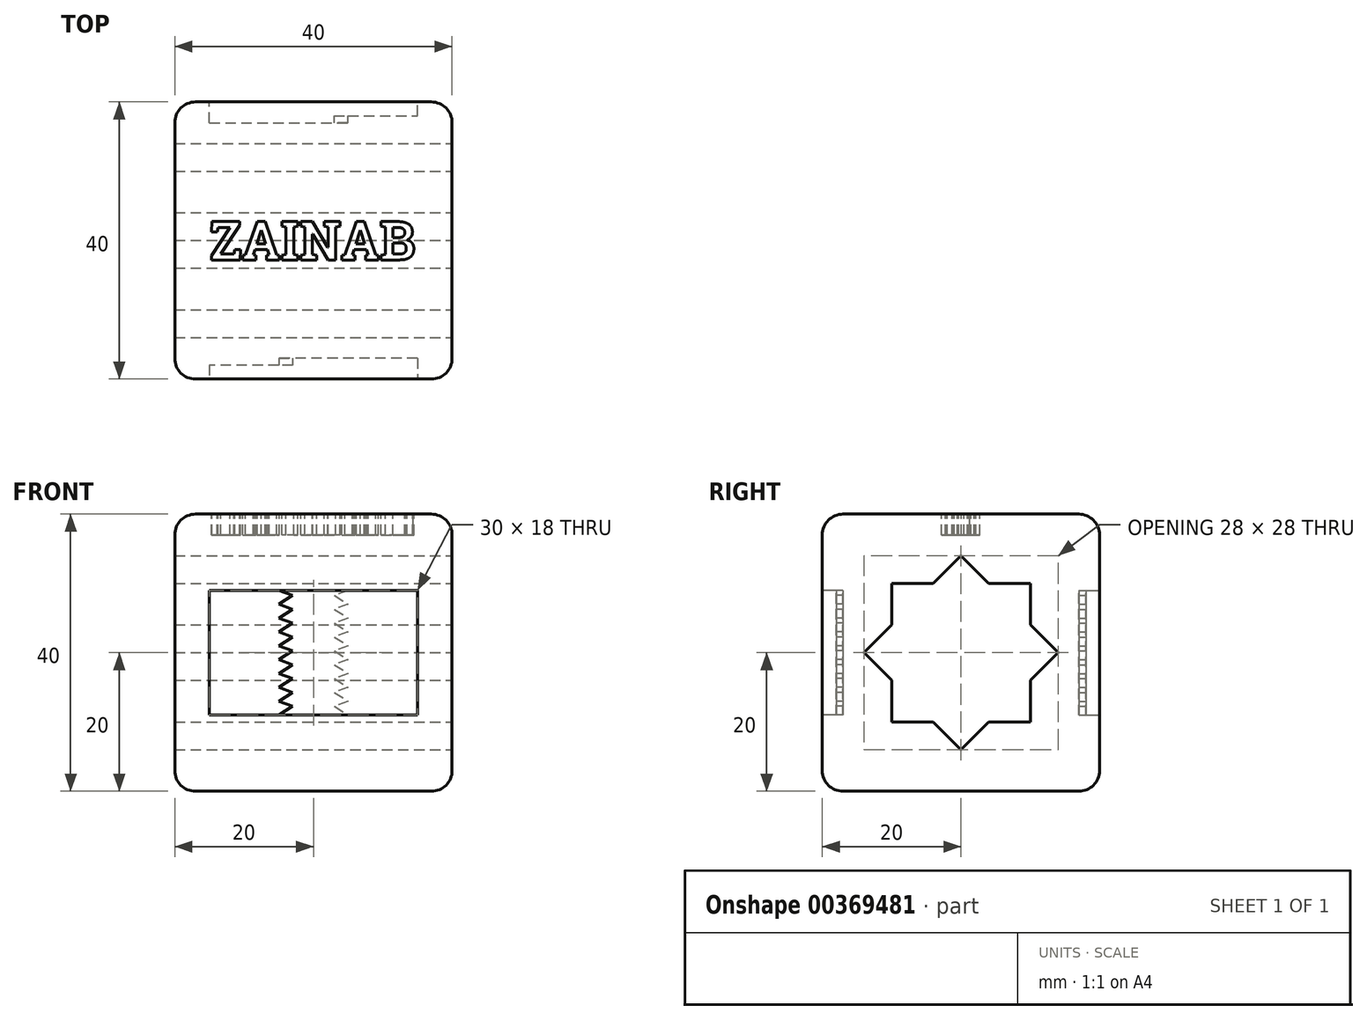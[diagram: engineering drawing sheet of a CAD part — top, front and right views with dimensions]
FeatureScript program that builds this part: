
annotation { "Feature Type Name" : "Feature", "Feature Type Description" : "" }
export const myFeature = defineFeature(function(context is Context, id is Id, definition is map)
    precondition{}
    {
        {
            var Q0;
            Q0=qCreatedBy(makeId("Front.planeOp"),FACE);
            var sketch = newSketch(context, id + "F0", { "sketchPlane" : qUnion([Q0])});
            skLineSegment(sketch, "E0.bottom", {"start": v(20, -20) * mm, "end": v(-20, -20) * mm});
            skLineSegment(sketch, "E0.top", {"start": v(20, 20) * mm, "end": v(-20, 20) * mm});
            skLineSegment(sketch, "E0.left", {"start": v(20, -20) * mm, "end": v(20, 20) * mm});
            skLineSegment(sketch, "E0.right", {"start": v(-20, -20) * mm, "end": v(-20, 20) * mm});
            skPoint(sketch, "E0.middle", {"position": v(0, 0) * mm});
            skSolve(sketch);
        }
        {
            var Q0;
            Q0 = qSketchRegion(id + "F0", true);
            extrude(context, id + "F1", {"entities" : qUnion([Q0]), "endBound" : BoundingType.SYMMETRIC, "depth" : 40 * mm});
        }
        {
            var Q0;
            Q0=makeQuery(id+"F1.opExtrude","CAP_EDGE",EDGE,{"disambiguationData":[OSD([sQuery(id+"F0.wireOp",EDGE,"E0.top")])],"isStart":false});
            var Q1;
            Q1=makeQuery(id+"F1.opExtrude","SWEPT_EDGE",EDGE,{"disambiguationData":[OSD([sQuery(id+"F0.wireOp",EDGE,"E0.top"),sQuery(id+"F0.wireOp",EDGE,"E0.left")])]});
            var Q2;
            Q2=makeQuery(id+"F1.opExtrude","CAP_EDGE",EDGE,{"disambiguationData":[OSD([sQuery(id+"F0.wireOp",EDGE,"E0.top")])],"isStart":true});
            var Q3;
            Q3=makeQuery(id+"F1.opExtrude","SWEPT_FACE",FACE,{"disambiguationData":[OSD([sQuery(id+"F0.wireOp",EDGE,"E0.top")])]});
            var Q4;
            Q4=makeQuery(id+"F1.opExtrude","SWEPT_EDGE",EDGE,{"disambiguationData":[OSD([sQuery(id+"F0.wireOp",EDGE,"E0.bottom"),sQuery(id+"F0.wireOp",EDGE,"E0.left")])]});
            var Q5;
            Q5=makeQuery(id+"F1.opExtrude","CAP_EDGE",EDGE,{"disambiguationData":[OSD([sQuery(id+"F0.wireOp",EDGE,"E0.left")])],"isStart":true});
            var Q6;
            Q6=makeQuery(id+"F1.opExtrude","CAP_EDGE",EDGE,{"disambiguationData":[OSD([sQuery(id+"F0.wireOp",EDGE,"E0.left")])],"isStart":false});
            var Q7;
            Q7=makeQuery(id+"F1.opExtrude","CAP_EDGE",EDGE,{"disambiguationData":[OSD([sQuery(id+"F0.wireOp",EDGE,"E0.bottom")])],"isStart":false});
            var Q8;
            Q8=makeQuery(id+"F1.opExtrude","CAP_EDGE",EDGE,{"disambiguationData":[OSD([sQuery(id+"F0.wireOp",EDGE,"E0.right")])],"isStart":false});
            var Q9;
            Q9=makeQuery(id+"F1.opExtrude","SWEPT_EDGE",EDGE,{"disambiguationData":[OSD([sQuery(id+"F0.wireOp",EDGE,"E0.bottom"),sQuery(id+"F0.wireOp",EDGE,"E0.right")])]});
            var Q10;
            Q10=makeQuery(id+"F1.opExtrude","CAP_EDGE",EDGE,{"disambiguationData":[OSD([sQuery(id+"F0.wireOp",EDGE,"E0.right")])],"isStart":true});
            var Q11;
            Q11=makeQuery(id+"F1.opExtrude","CAP_EDGE",EDGE,{"disambiguationData":[OSD([sQuery(id+"F0.wireOp",EDGE,"E0.bottom")])],"isStart":true});
            fillet(context, id + "F2", {"entities" : qUnion([Q0, Q1, Q2, Q3, Q4, Q5, Q6, Q7, Q8, Q9, Q10, Q11]), "radius" : 3 * mm, "tangentPropagation" : true, "allowEdgeOverflow" : false});
        }
        {
            var Q0;
            Q0=makeQuery(id+"F1.opExtrude","SWEPT_FACE",FACE,{"disambiguationData":[OSD([sQuery(id+"F0.wireOp",EDGE,"E0.left")])]});
            var sketch = newSketch(context, id + "F3", { "sketchPlane" : qUnion([Q0])});
            skLineSegment(sketch, "E1.bottom", {"start": v(10, -10) * mm, "end": v(-10, -10) * mm});
            skLineSegment(sketch, "E1.top", {"start": v(10, 10) * mm, "end": v(-10, 10) * mm});
            skLineSegment(sketch, "E1.left", {"start": v(10, -10) * mm, "end": v(10, 10) * mm});
            skLineSegment(sketch, "E1.right", {"start": v(-10, -10) * mm, "end": v(-10, 10) * mm});
            skPoint(sketch, "E1.middle", {"position": v(0, 0) * mm});
            skCircle(sketch, "E2.cCircle", {"center": v(0, 0) * mm, "radius": 14 * mm, "construction": true});
            skPoint(sketch, "E2.cCircle.perimeterSnap0", {"position": v(0, 10) * mm});
            skLineSegment(sketch, "E2.0", {"start": v(0, 14) * mm, "end": v(14, 0) * mm});
            skPoint(sketch, "E2.0.startSnap0", {"position": v(0, 10) * mm});
            skLineSegment(sketch, "E2.1", {"start": v(14, 0) * mm, "end": v(0, -14) * mm});
            skLineSegment(sketch, "E2.2", {"start": v(0, -14) * mm, "end": v(-14, 0) * mm});
            skLineSegment(sketch, "E2.3", {"start": v(-14, 0) * mm, "end": v(0, 14) * mm});
            skSolve(sketch);
        }
        {
            var Q0;
            Q0 = qSketchRegion(id + "F3", true);
            extrude(context, id + "F4", {"entities" : qUnion([Q0]), "operationType" : NewBodyOperationType.REMOVE, "endBound" : BoundingType.THROUGH_ALL, "oppositeDirection" : true, "depth" : 25 * mm});
        }
        {
            var Q0;
            Q0=makeQuery(id+"F1.opExtrude","CAP_FACE",FACE,{"disambiguationData":[OSD([sQuery(id+"F0.wireOp",EDGE,"E0.bottom"),sQuery(id+"F0.wireOp",EDGE,"E0.top"),sQuery(id+"F0.wireOp",EDGE,"E0.left"),sQuery(id+"F0.wireOp",EDGE,"E0.right")])],"isStart":false});
            var sketch = newSketch(context, id + "F5", { "sketchPlane" : qUnion([Q0])});
            skLineSegment(sketch, "E3.bottom", {"start": v(15, -9) * mm, "end": v(-15, -9) * mm});
            skLineSegment(sketch, "E3.top", {"start": v(15, 9) * mm, "end": v(-15, 9) * mm});
            skLineSegment(sketch, "E3.left", {"start": v(15, -9) * mm, "end": v(15, 9) * mm});
            skLineSegment(sketch, "E3.right", {"start": v(-15, -9) * mm, "end": v(-15, 9) * mm});
            skPoint(sketch, "E3.middle", {"position": v(0, 0) * mm});
            skLineSegment(sketch, "E4", {"start": v(-5, 9) * mm, "end": v(-3, 8.27) * mm});
            skLineSegment(sketch, "E5", {"start": v(-3, 8.27) * mm, "end": v(-5, 7) * mm});
            skLineSegment(sketch, "E6.0.1.0", {"start": v(-5, 7) * mm, "end": v(-3, 6.27) * mm});
            skLineSegment(sketch, "E6.0.1.1", {"start": v(-3, 6.27) * mm, "end": v(-5, 5) * mm});
            skLineSegment(sketch, "E6.0.2.0", {"start": v(-5, 5) * mm, "end": v(-3, 4.27) * mm});
            skLineSegment(sketch, "E6.0.2.1", {"start": v(-3, 4.27) * mm, "end": v(-5, 3) * mm});
            skLineSegment(sketch, "E6.0.3.0", {"start": v(-5, 3) * mm, "end": v(-3, 2.27) * mm});
            skLineSegment(sketch, "E6.0.3.1", {"start": v(-3, 2.27) * mm, "end": v(-5, 1) * mm});
            skLineSegment(sketch, "E6.0.4.0", {"start": v(-5, 1) * mm, "end": v(-3, 0.27) * mm});
            skLineSegment(sketch, "E6.0.4.1", {"start": v(-3, 0.27) * mm, "end": v(-5, -1) * mm});
            skLineSegment(sketch, "E6.0.5.0", {"start": v(-5, -1) * mm, "end": v(-3, -1.73) * mm});
            skLineSegment(sketch, "E6.0.5.1", {"start": v(-3, -1.73) * mm, "end": v(-5, -3) * mm});
            skLineSegment(sketch, "E6.0.6.0", {"start": v(-5, -3) * mm, "end": v(-3, -3.73) * mm});
            skLineSegment(sketch, "E6.0.6.1", {"start": v(-3, -3.73) * mm, "end": v(-5, -5) * mm});
            skLineSegment(sketch, "E6.0.7.0", {"start": v(-5, -5) * mm, "end": v(-3, -5.73) * mm});
            skLineSegment(sketch, "E6.0.7.1", {"start": v(-3, -5.73) * mm, "end": v(-5, -7) * mm});
            skLineSegment(sketch, "E6.0.8.0", {"start": v(-5, -7) * mm, "end": v(-3, -7.73) * mm});
            skLineSegment(sketch, "E6.0.8.1", {"start": v(-3, -7.73) * mm, "end": v(-5, -9) * mm});
            skLineSegment(sketch, "E6.direction1", {"start": v(-5, 9) * mm, "end": v(20, 9) * mm, "construction": true});
            skLineSegment(sketch, "E6.direction2", {"start": v(-5, 9) * mm, "end": v(-5, 7) * mm, "construction": true});
            skSolve(sketch);
        }
        {
            var Q0;
            {var subQ0=sQuery(id+"F5.wireOp",EDGE,"E3.right");Q0=makeQuery(id+"F5.imprint","IMPRINT",FACE,{"disambiguationData":[TD([[makeQuery(id+"F5.imprint","IMPRINT",EDGE,{"derivedFrom":subQ0}),-1.0]])]});}
            extrude(context, id + "F6", {"entities" : qUnion([Q0]), "operationType" : NewBodyOperationType.REMOVE, "oppositeDirection" : true, "depth" : 2 * mm});
        }
        {
            var Q0;
            {var subQ0=sQuery(id+"F5.wireOp",EDGE,"E3.left");Q0=makeQuery(id+"F5.imprint","IMPRINT",FACE,{"disambiguationData":[TD([[makeQuery(id+"F5.imprint","IMPRINT",EDGE,{"derivedFrom":subQ0}),1.0]])]});}
            extrude(context, id + "F7", {"entities" : qUnion([Q0]), "operationType" : NewBodyOperationType.REMOVE, "oppositeDirection" : true, "depth" : 3 * mm});
        }
        {
            var Q0;
            Q0=makeQuery(id+"F1.opExtrude","CAP_FACE",FACE,{"disambiguationData":[OSD([sQuery(id+"F0.wireOp",EDGE,"E0.bottom"),sQuery(id+"F0.wireOp",EDGE,"E0.top"),sQuery(id+"F0.wireOp",EDGE,"E0.left"),sQuery(id+"F0.wireOp",EDGE,"E0.right")])],"isStart":true});
            var sketch = newSketch(context, id + "F8", { "sketchPlane" : qUnion([Q0])});
            skLineSegment(sketch, "E7.bottom", {"start": v(15, -9) * mm, "end": v(-15, -9) * mm});
            skLineSegment(sketch, "E7.top", {"start": v(15, 9) * mm, "end": v(-15, 9) * mm});
            skLineSegment(sketch, "E7.left", {"start": v(15, -9) * mm, "end": v(15, 9) * mm});
            skLineSegment(sketch, "E7.right", {"start": v(-15, -9) * mm, "end": v(-15, 9) * mm});
            skPoint(sketch, "E7.middle", {"position": v(0, 0) * mm});
            skLineSegment(sketch, "E8", {"start": v(-5, 9) * mm, "end": v(-3, 8.27) * mm});
            skLineSegment(sketch, "E9", {"start": v(-3, 8.27) * mm, "end": v(-5, 7) * mm});
            skLineSegment(sketch, "E10.0.1.0", {"start": v(-5, 7) * mm, "end": v(-3, 6.27) * mm});
            skLineSegment(sketch, "E10.0.1.1", {"start": v(-3, 6.27) * mm, "end": v(-5, 5) * mm});
            skLineSegment(sketch, "E10.0.2.0", {"start": v(-5, 5) * mm, "end": v(-3, 4.27) * mm});
            skLineSegment(sketch, "E10.0.2.1", {"start": v(-3, 4.27) * mm, "end": v(-5, 3) * mm});
            skLineSegment(sketch, "E10.0.3.0", {"start": v(-5, 3) * mm, "end": v(-3, 2.27) * mm});
            skLineSegment(sketch, "E10.0.3.1", {"start": v(-3, 2.27) * mm, "end": v(-5, 1) * mm});
            skLineSegment(sketch, "E10.0.4.0", {"start": v(-5, 1) * mm, "end": v(-3, 0.27) * mm});
            skLineSegment(sketch, "E10.0.4.1", {"start": v(-3, 0.27) * mm, "end": v(-5, -1) * mm});
            skLineSegment(sketch, "E10.0.5.0", {"start": v(-5, -1) * mm, "end": v(-3, -1.73) * mm});
            skLineSegment(sketch, "E10.0.5.1", {"start": v(-3, -1.73) * mm, "end": v(-5, -3) * mm});
            skLineSegment(sketch, "E10.0.6.0", {"start": v(-5, -3) * mm, "end": v(-3, -3.73) * mm});
            skLineSegment(sketch, "E10.0.6.1", {"start": v(-3, -3.73) * mm, "end": v(-5, -5) * mm});
            skLineSegment(sketch, "E10.0.7.0", {"start": v(-5, -5) * mm, "end": v(-3, -5.73) * mm});
            skLineSegment(sketch, "E10.0.7.1", {"start": v(-3, -5.73) * mm, "end": v(-5, -7) * mm});
            skLineSegment(sketch, "E10.0.8.0", {"start": v(-5, -7) * mm, "end": v(-3, -7.73) * mm});
            skLineSegment(sketch, "E10.0.8.1", {"start": v(-3, -7.73) * mm, "end": v(-5, -9) * mm});
            skLineSegment(sketch, "E10.direction1", {"start": v(-5, 9) * mm, "end": v(20, 9) * mm, "construction": true});
            skLineSegment(sketch, "E10.direction2", {"start": v(-5, 9) * mm, "end": v(-5, 7) * mm, "construction": true});
            skSolve(sketch);
        }
        {
            var Q0;
            {var subQ0=sQuery(id+"F8.wireOp",EDGE,"E7.right");Q0=makeQuery(id+"F8.imprint","IMPRINT",FACE,{"disambiguationData":[TD([[makeQuery(id+"F8.imprint","IMPRINT",EDGE,{"derivedFrom":subQ0}),-1.0]])]});}
            extrude(context, id + "F9", {"entities" : qUnion([Q0]), "operationType" : NewBodyOperationType.REMOVE, "oppositeDirection" : true, "depth" : 2 * mm});
        }
        {
            var Q0;
            {var subQ0=sQuery(id+"F8.wireOp",EDGE,"E7.left");Q0=makeQuery(id+"F8.imprint","IMPRINT",FACE,{"disambiguationData":[TD([[makeQuery(id+"F8.imprint","IMPRINT",EDGE,{"derivedFrom":subQ0}),1.0]])]});}
            extrude(context, id + "F10", {"entities" : qUnion([Q0]), "operationType" : NewBodyOperationType.REMOVE, "oppositeDirection" : true, "depth" : 3 * mm});
        }
        {
            var Q0;
            Q0=makeQuery(id+"F1.opExtrude","SWEPT_FACE",FACE,{"disambiguationData":[OSD([sQuery(id+"F0.wireOp",EDGE,"E0.top")])]});
            var sketch = newSketch(context, id + "F11", { "sketchPlane" : qUnion([Q0])});
            skText(sketch, "E11", { "text": "ZAINAB", "fontName": "RobotoSlab-Bold.ttf"});
            skPoint(sketch, "E12", {"position": v(0, 2.8) * mm});
            skPoint(sketch, "E13", {"position": v(15, 0) * mm});
            const initialGuessF11  = {"E11": [-0.015, -0.0028, 1, 0, 0.0056]};
            skSetInitialGuess(sketch, initialGuessF11);
            skSolve(sketch);
        }
        {
            var Q0;
            Q0 = qSketchRegion(id + "F11", true);
            extrude(context, id + "F12", {"entities" : qUnion([Q0]), "operationType" : NewBodyOperationType.REMOVE, "oppositeDirection" : true, "depth" : 3 * mm});
        }
    });
